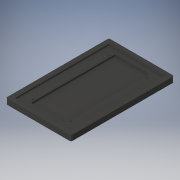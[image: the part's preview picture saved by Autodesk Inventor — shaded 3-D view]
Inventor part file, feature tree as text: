
AUTODESK INVENTOR PART (.ipt)
format: ipt  version: 2019.4 (Build 234330000, 330)  size: 139,264 bytes
history: native  units: in
note: dims shown in document units (in); Inventor stores cm internally (conversion verified against a paired STEP export)
features: sketch x4, extrude x3, hole x1, fillet x1
ambient origin geometry x8: Origin, YZ Plane, XZ Plane, XY Plane, X Axis, Y Axis, Z Axis, Center Point
bodies: Solid1 (feature_tree)
feature tree (9):
  extrude  "Extrusion1"  Depth=6.0in
  extrude  "Extrusion2"  Depth=8.625in
  extrude  "Extrusion3"  Depth=0.125in TaperAngle=0.0deg
  hole  "Hole1"  [1 undecoded]
  fillet  "Fillet1"  Radius=0.15in
  sketch  "Sketch1"  dims[d0=9.5in d1=6.0in]
  sketch  "Sketch2"  dims[d2=0.5in d3=0.0in d4=8.625in]
  sketch  "Sketch3"  dims[d5=5.125in d6=0.125in d7=0.0in]
  sketch  "Sketch4"  dims[d8=0.45in d9=1.0in d10=0.15in d11=0.0in d12=0.8125in d13=0.8125in d14=0.7874in d16=7.0in d17=0.7874in d19=3.5in d22=0.134in d23=0.125in d24=0.248in d25=0.25in d26=90.0deg d27=0.1875in d28=0.8108in d29=0.125in]
note: 1 required parameter value undecoded (feature->parameter linkage not recoverable at this tier; creation-order binding heuristic only, values carry confidence <= 0.55)
